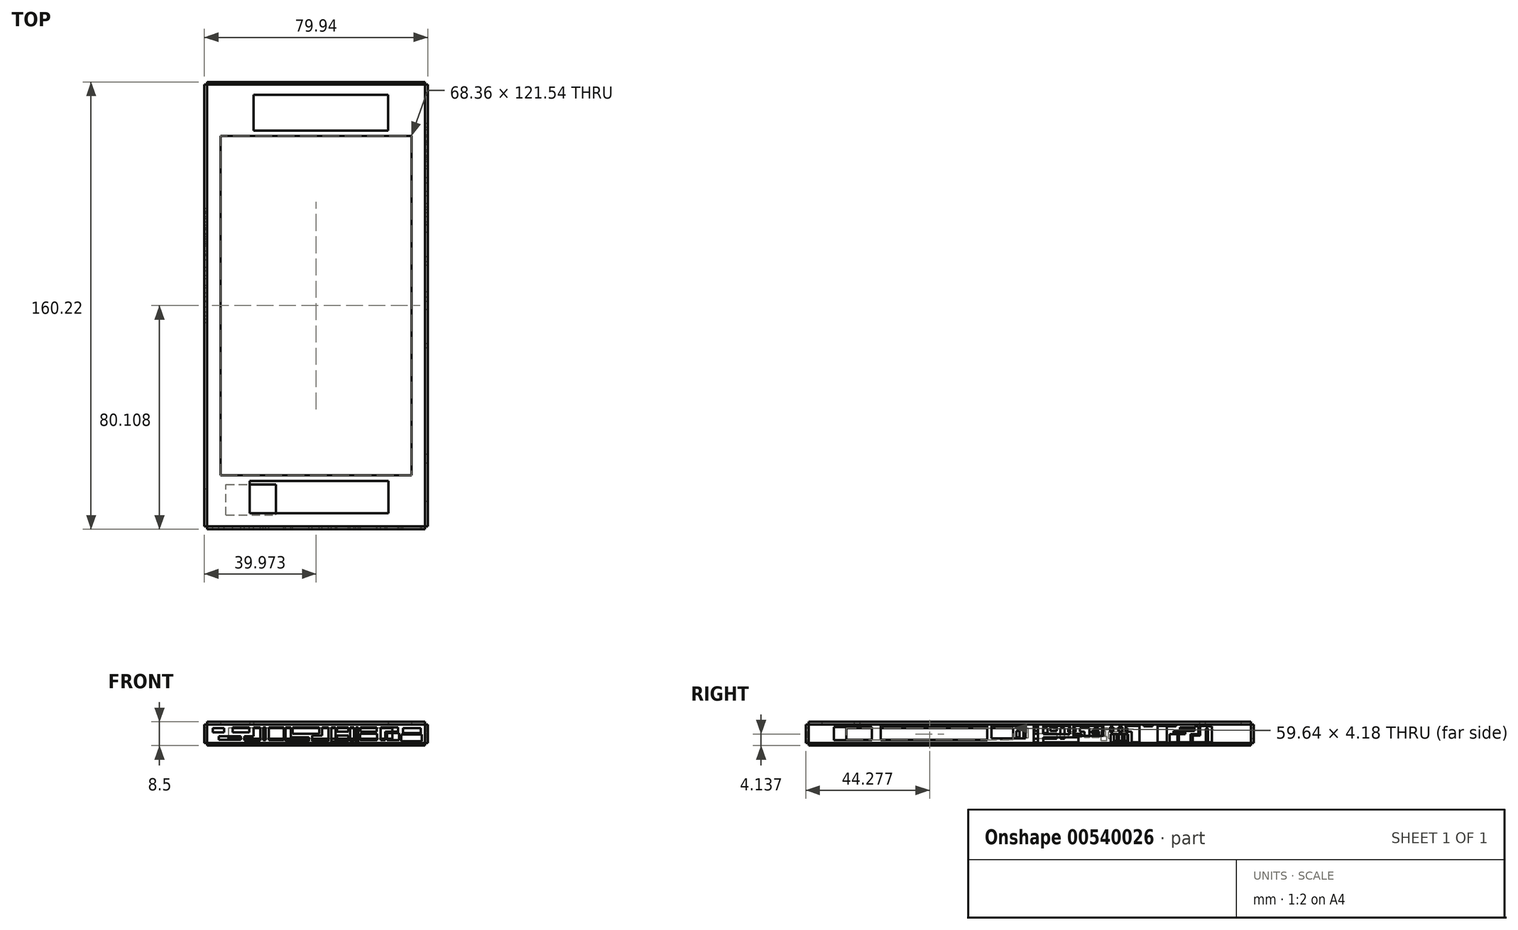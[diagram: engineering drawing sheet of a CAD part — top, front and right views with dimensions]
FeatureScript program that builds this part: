
annotation { "Feature Type Name" : "Feature", "Feature Type Description" : "" }
export const myFeature = defineFeature(function(context is Context, id is Id, definition is map)
    precondition{}
    {
        {
            var Q0;
            Q0=qCreatedBy(makeId("Top.planeOp"),FACE);
            var sketch = newSketch(context, id + "F0", { "sketchPlane" : qUnion([Q0])});
            skLineSegment(sketch, "E0.bottom", {"start": v(115.76, -47.1) * mm, "end": v(47.4, -47.1) * mm});
            skLineSegment(sketch, "E0.top", {"start": v(115.76, 74.45) * mm, "end": v(47.4, 74.45) * mm});
            skLineSegment(sketch, "E0.left", {"start": v(115.76, -47.1) * mm, "end": v(115.76, 74.45) * mm});
            skLineSegment(sketch, "E0.right", {"start": v(47.4, -47.1) * mm, "end": v(47.4, 74.45) * mm});
            skLineSegment(sketch, "E1.bottom", {"start": v(120.55, -65.43) * mm, "end": v(42.61, -65.43) * mm});
            skLineSegment(sketch, "E1.top", {"start": v(120.55, 92.79) * mm, "end": v(42.61, 92.79) * mm});
            skLineSegment(sketch, "E1.left", {"start": v(120.55, -65.43) * mm, "end": v(120.55, 92.79) * mm});
            skLineSegment(sketch, "E1.right", {"start": v(42.61, -65.43) * mm, "end": v(42.61, 92.79) * mm});
            skPoint(sketch, "E2", {"position": v(81.58, 13.68) * mm});
            skPoint(sketch, "E3", {"position": v(81.58, 74.45) * mm});
            skPoint(sketch, "E4", {"position": v(47.4, 13.68) * mm});
            skPoint(sketch, "E5", {"position": v(81.58, -65.43) * mm});
            skPoint(sketch, "E6", {"position": v(42.61, 13.68) * mm});
            skLineSegment(sketch, "E7.bottom", {"start": v(44.35, 91.05) * mm, "end": v(118.82, 91.05) * mm});
            skLineSegment(sketch, "E7.top", {"start": v(44.35, -63.7) * mm, "end": v(118.82, -63.7) * mm});
            skLineSegment(sketch, "E7.left", {"start": v(44.35, 91.05) * mm, "end": v(44.35, -63.7) * mm});
            skLineSegment(sketch, "E7.right", {"start": v(118.82, 91.05) * mm, "end": v(118.82, -63.7) * mm});
            skPoint(sketch, "E8", {"position": v(81.58, -63.7) * mm});
            skPoint(sketch, "E9", {"position": v(118.82, 13.68) * mm});
            skLineSegment(sketch, "E10.bottom", {"start": v(59.18, 89.21) * mm, "end": v(107.32, 89.21) * mm});
            skLineSegment(sketch, "E10.top", {"start": v(59.18, 76.37) * mm, "end": v(107.32, 76.37) * mm});
            skLineSegment(sketch, "E10.left", {"start": v(59.18, 89.21) * mm, "end": v(59.18, 76.37) * mm});
            skLineSegment(sketch, "E10.right", {"start": v(107.32, 89.21) * mm, "end": v(107.32, 76.37) * mm});
            skLineSegment(sketch, "E11.bottom", {"start": v(57.84, -49.13) * mm, "end": v(107.53, -49.13) * mm});
            skLineSegment(sketch, "E11.top", {"start": v(57.84, -60.7) * mm, "end": v(107.53, -60.7) * mm});
            skLineSegment(sketch, "E11.left", {"start": v(57.84, -49.13) * mm, "end": v(57.84, -60.7) * mm});
            skLineSegment(sketch, "E11.right", {"start": v(107.53, -49.13) * mm, "end": v(107.53, -60.7) * mm});
            skSolve(sketch);
        }
        {
            var Q0;
            Q0=makeQuery(id+"F0.imprint","IMPRINT",FACE,{"disambiguationData":[TD([[makeQuery(id+"F0.imprint","IMPRINT",EDGE,{"derivedFrom":sQuery(id+"F0.wireOp",EDGE,"E0.bottom")}),1.0]])]});
            var Q1;
            Q1=makeQuery(id+"F0.imprint","IMPRINT",FACE,{"disambiguationData":[TD([[makeQuery(id+"F0.imprint","IMPRINT",EDGE,{"derivedFrom":sQuery(id+"F0.wireOp",EDGE,"E1.bottom")}),-1.0]])]});
            extrude(context, id + "F1", {"entities" : qUnion([Q0, Q1]), "depth" : 1 * mm, "offsetDistance" : 25 * mm});
        }
        {
            var Q0;
            Q0=makeQuery(id+"F1.opExtrude","SWEPT_FACE",FACE,{"disambiguationData":[OSD([sQuery(id+"F0.wireOp",EDGE,"E1.left")])]});
            var sketch = newSketch(context, id + "F2", { "sketchPlane" : qUnion([Q0])});
            skLineSegment(sketch, "E12.bottom", {"start": v(-65.43, 1) * mm, "end": v(92.79, 1) * mm});
            skLineSegment(sketch, "E12.top", {"start": v(-65.43, -6.5) * mm, "end": v(92.79, -6.5) * mm});
            skLineSegment(sketch, "E12.left", {"start": v(-65.43, 1) * mm, "end": v(-65.43, -6.5) * mm});
            skLineSegment(sketch, "E12.right", {"start": v(92.79, 1) * mm, "end": v(92.79, -6.5) * mm});
            skLineSegment(sketch, "E13.bottom", {"start": v(-56.46, -0.8) * mm, "end": v(-42.84, -0.8) * mm});
            skLineSegment(sketch, "E13.top", {"start": v(-56.46, -5.5) * mm, "end": v(-42.84, -5.5) * mm});
            skLineSegment(sketch, "E13.left", {"start": v(-56.46, -0.8) * mm, "end": v(-56.46, -5.5) * mm});
            skLineSegment(sketch, "E13.right", {"start": v(-42.84, -0.8) * mm, "end": v(-42.84, -5.5) * mm});
            skLineSegment(sketch, "E14.bottom", {"start": v(-39.62, -0.51) * mm, "end": v(-1.52, -0.51) * mm});
            skLineSegment(sketch, "E14.top", {"start": v(-39.62, -5.6) * mm, "end": v(-1.52, -5.6) * mm});
            skLineSegment(sketch, "E14.left", {"start": v(-39.62, -0.51) * mm, "end": v(-39.62, -5.6) * mm});
            skLineSegment(sketch, "E14.right", {"start": v(-1.52, -0.51) * mm, "end": v(-1.52, -5.6) * mm});
            skLineSegment(sketch, "E15.bottom", {"start": v(0, -0.51) * mm, "end": v(12.2, -0.51) * mm});
            skLineSegment(sketch, "E15.top", {"start": v(0, -4.86) * mm, "end": v(12.2, -4.86) * mm});
            skLineSegment(sketch, "E15.left", {"start": v(0, -0.51) * mm, "end": v(0, -4.86) * mm});
            skLineSegment(sketch, "E15.right", {"start": v(12.2, -0.51) * mm, "end": v(12.2, -4.86) * mm});
            skLineSegment(sketch, "E16.bottom", {"start": v(15.07, -0.51) * mm, "end": v(16.6, -0.51) * mm});
            skLineSegment(sketch, "E16.top", {"start": v(15.07, -6.36) * mm, "end": v(16.6, -6.36) * mm});
            skLineSegment(sketch, "E16.left", {"start": v(15.07, -0.51) * mm, "end": v(15.07, -6.36) * mm});
            skLineSegment(sketch, "E16.right", {"start": v(16.6, -0.51) * mm, "end": v(16.6, -6.36) * mm});
            skLineSegment(sketch, "E17.bottom", {"start": v(18.51, -0.51) * mm, "end": v(28.08, -0.51) * mm});
            skLineSegment(sketch, "E17.top", {"start": v(18.51, -3.32) * mm, "end": v(28.08, -3.32) * mm});
            skLineSegment(sketch, "E17.left", {"start": v(18.51, -0.51) * mm, "end": v(18.51, -3.32) * mm});
            skLineSegment(sketch, "E17.right", {"start": v(28.08, -0.51) * mm, "end": v(28.08, -3.32) * mm});
            skLineSegment(sketch, "E18.bottom", {"start": v(18.51, -6.36) * mm, "end": v(31.14, -6.36) * mm});
            skLineSegment(sketch, "E18.top", {"start": v(18.51, -4.47) * mm, "end": v(31.14, -4.47) * mm});
            skLineSegment(sketch, "E18.left", {"start": v(18.51, -6.36) * mm, "end": v(18.51, -4.47) * mm});
            skLineSegment(sketch, "E18.right", {"start": v(31.14, -6.36) * mm, "end": v(31.14, -4.47) * mm});
            skLineSegment(sketch, "E19.bottom", {"start": v(29.37, -3.96) * mm, "end": v(39.95, -3.96) * mm});
            skLineSegment(sketch, "E19.top", {"start": v(29.37, -0.51) * mm, "end": v(39.95, -0.51) * mm});
            skLineSegment(sketch, "E19.left", {"start": v(29.37, -3.96) * mm, "end": v(29.37, -0.51) * mm});
            skLineSegment(sketch, "E19.right", {"start": v(39.95, -3.96) * mm, "end": v(39.95, -0.51) * mm});
            skLineSegment(sketch, "E20.bottom", {"start": v(42.63, -3.32) * mm, "end": v(48.85, -3.32) * mm});
            skLineSegment(sketch, "E20.top", {"start": v(42.63, -6.36) * mm, "end": v(48.85, -6.36) * mm});
            skLineSegment(sketch, "E20.left", {"start": v(42.63, -3.32) * mm, "end": v(42.63, -6.36) * mm});
            skLineSegment(sketch, "E20.right", {"start": v(48.85, -3.32) * mm, "end": v(48.85, -6.36) * mm});
            skLineSegment(sketch, "E21.bottom", {"start": v(42.43, -0.84) * mm, "end": v(43.58, -0.84) * mm});
            skLineSegment(sketch, "E21.top", {"start": v(42.43, -2.56) * mm, "end": v(43.58, -2.56) * mm});
            skLineSegment(sketch, "E21.left", {"start": v(42.43, -0.84) * mm, "end": v(42.43, -2.56) * mm});
            skLineSegment(sketch, "E21.right", {"start": v(43.58, -0.84) * mm, "end": v(43.58, -2.56) * mm});
            skLineSegment(sketch, "E22.bottom", {"start": v(45.5, -0.84) * mm, "end": v(46.84, -0.84) * mm});
            skLineSegment(sketch, "E22.top", {"start": v(45.5, -2.46) * mm, "end": v(46.84, -2.46) * mm});
            skLineSegment(sketch, "E22.left", {"start": v(45.5, -0.84) * mm, "end": v(45.5, -2.46) * mm});
            skLineSegment(sketch, "E22.right", {"start": v(46.84, -0.84) * mm, "end": v(46.84, -2.46) * mm});
            skLineSegment(sketch, "E23.bottom", {"start": v(47.98, -0.51) * mm, "end": v(52.96, -0.51) * mm});
            skLineSegment(sketch, "E23.top", {"start": v(47.98, -2.56) * mm, "end": v(52.96, -2.56) * mm});
            skLineSegment(sketch, "E23.left", {"start": v(47.98, -0.51) * mm, "end": v(47.98, -2.56) * mm});
            skLineSegment(sketch, "E23.right", {"start": v(52.96, -0.51) * mm, "end": v(52.96, -2.56) * mm});
            skLineSegment(sketch, "E24.top", {"start": v(52.96, -6.36) * mm, "end": v(50.18, -6.36) * mm});
            skLineSegment(sketch, "E24.left", {"start": v(52.96, -2.56) * mm, "end": v(52.96, -6.36) * mm});
            skLineSegment(sketch, "E24.right", {"start": v(50.18, -2.56) * mm, "end": v(50.18, -6.36) * mm});
            skLineSegment(sketch, "E25.bottom", {"start": v(54.46, -0.51) * mm, "end": v(57.6, -0.51) * mm});
            skLineSegment(sketch, "E25.top", {"start": v(54.46, -0.65) * mm, "end": v(57.6, -0.65) * mm});
            skLineSegment(sketch, "E25.left", {"start": v(54.46, -0.65) * mm, "end": v(54.46, -0.51) * mm});
            skLineSegment(sketch, "E25.right", {"start": v(57.6, -0.65) * mm, "end": v(57.6, -0.51) * mm});
            skLineSegment(sketch, "E26.top", {"start": v(54.46, -6.36) * mm, "end": v(57.6, -6.36) * mm});
            skLineSegment(sketch, "E26.left", {"start": v(54.46, -0.51) * mm, "end": v(54.46, -6.36) * mm});
            skLineSegment(sketch, "E26.right", {"start": v(57.6, -1.64) * mm, "end": v(57.6, -6.36) * mm});
            skLineSegment(sketch, "E27.bottom", {"start": v(59.39, -0.65) * mm, "end": v(65.96, -0.65) * mm});
            skLineSegment(sketch, "E27.top", {"start": v(59.39, -0.51) * mm, "end": v(65.96, -0.51) * mm});
            skLineSegment(sketch, "E27.left", {"start": v(59.39, -0.51) * mm, "end": v(59.39, -0.65) * mm});
            skLineSegment(sketch, "E27.right", {"start": v(65.96, -0.51) * mm, "end": v(65.96, -0.65) * mm});
            skPoint(sketch, "E28.oppositeSnap0", {"position": v(62.67, -0.51) * mm});
            skLineSegment(sketch, "E28.bottom", {"start": v(59.39, -0.51) * mm, "end": v(62.67, -0.51) * mm});
            skLineSegment(sketch, "E28.top", {"start": v(59.39, -6.36) * mm, "end": v(62.67, -6.36) * mm});
            skLineSegment(sketch, "E28.left", {"start": v(59.39, -0.51) * mm, "end": v(59.39, -6.36) * mm});
            skLineSegment(sketch, "E28.right", {"start": v(62.67, -0.51) * mm, "end": v(62.67, -6.36) * mm});
            skPoint(sketch, "E29.firstSnap0", {"position": v(62.67, -3.44) * mm});
            skLineSegment(sketch, "E29.bottom", {"start": v(63.68, -3.44) * mm, "end": v(66.53, -3.44) * mm});
            skLineSegment(sketch, "E29.top", {"start": v(63.68, -6.36) * mm, "end": v(66.53, -6.36) * mm});
            skLineSegment(sketch, "E29.left", {"start": v(63.68, -3.44) * mm, "end": v(63.68, -6.36) * mm});
            skLineSegment(sketch, "E29.right", {"start": v(66.53, -3.44) * mm, "end": v(66.53, -6.36) * mm});
            skPoint(sketch, "E30.firstSnap0", {"position": v(65.1, -3.44) * mm});
            skLineSegment(sketch, "E30.bottom", {"start": v(65.1, -2.3) * mm, "end": v(68.7, -2.3) * mm});
            skLineSegment(sketch, "E30.top", {"start": v(65.1, -3.15) * mm, "end": v(68.7, -3.15) * mm});
            skLineSegment(sketch, "E30.left", {"start": v(65.1, -2.3) * mm, "end": v(65.1, -3.15) * mm});
            skLineSegment(sketch, "E30.right", {"start": v(68.7, -2.3) * mm, "end": v(68.7, -3.15) * mm});
            skLineSegment(sketch, "E31.bottom", {"start": v(67.44, -0.96) * mm, "end": v(72.16, -0.96) * mm});
            skLineSegment(sketch, "E31.top", {"start": v(67.44, -1.88) * mm, "end": v(72.16, -1.88) * mm});
            skLineSegment(sketch, "E31.left", {"start": v(67.44, -0.96) * mm, "end": v(67.44, -1.88) * mm});
            skLineSegment(sketch, "E31.right", {"start": v(72.16, -0.96) * mm, "end": v(72.16, -1.88) * mm});
            skLineSegment(sketch, "E32.bottom", {"start": v(67, -3.44) * mm, "end": v(71.26, -3.44) * mm});
            skLineSegment(sketch, "E32.top", {"start": v(67, -6.36) * mm, "end": v(71.26, -6.36) * mm});
            skLineSegment(sketch, "E32.left", {"start": v(67, -3.44) * mm, "end": v(67, -6.36) * mm});
            skLineSegment(sketch, "E32.right", {"start": v(71.26, -3.44) * mm, "end": v(71.26, -6.36) * mm});
            skLineSegment(sketch, "E33.bottom", {"start": v(71.26, -3.44) * mm, "end": v(69.33, -3.44) * mm});
            skLineSegment(sketch, "E33.top", {"start": v(71.26, -2.22) * mm, "end": v(69.33, -2.22) * mm});
            skLineSegment(sketch, "E33.left", {"start": v(71.26, -3.44) * mm, "end": v(71.26, -2.22) * mm});
            skLineSegment(sketch, "E33.right", {"start": v(69.33, -3.44) * mm, "end": v(69.33, -2.22) * mm});
            skLineSegment(sketch, "E34.bottom", {"start": v(71.26, -2.22) * mm, "end": v(74.03, -2.22) * mm});
            skLineSegment(sketch, "E34.top", {"start": v(71.26, -3.44) * mm, "end": v(74.03, -3.44) * mm});
            skLineSegment(sketch, "E34.left", {"start": v(71.26, -2.22) * mm, "end": v(71.26, -3.44) * mm});
            skLineSegment(sketch, "E34.right", {"start": v(74.03, -2.22) * mm, "end": v(74.03, -3.44) * mm});
            skLineSegment(sketch, "E35.bottom", {"start": v(74.03, -2.22) * mm, "end": v(72.68, -2.22) * mm});
            skLineSegment(sketch, "E35.top", {"start": v(74.03, -0.65) * mm, "end": v(72.68, -0.65) * mm});
            skLineSegment(sketch, "E35.left", {"start": v(74.03, -2.22) * mm, "end": v(74.03, -0.65) * mm});
            skLineSegment(sketch, "E35.right", {"start": v(72.68, -2.22) * mm, "end": v(72.68, -0.65) * mm});
            skLineSegment(sketch, "E36.bottom", {"start": v(71.94, -3.84) * mm, "end": v(76.64, -3.84) * mm});
            skLineSegment(sketch, "E36.top", {"start": v(71.94, -6.36) * mm, "end": v(76.64, -6.36) * mm});
            skLineSegment(sketch, "E36.left", {"start": v(71.94, -3.84) * mm, "end": v(71.94, -6.36) * mm});
            skLineSegment(sketch, "E36.right", {"start": v(76.64, -3.84) * mm, "end": v(76.64, -6.36) * mm});
            skLineSegment(sketch, "E37.bottom", {"start": v(76.64, -3.84) * mm, "end": v(74.68, -3.84) * mm});
            skLineSegment(sketch, "E37.top", {"start": v(76.64, -0.51) * mm, "end": v(74.68, -0.51) * mm});
            skLineSegment(sketch, "E37.left", {"start": v(76.64, -3.84) * mm, "end": v(76.64, -0.51) * mm});
            skLineSegment(sketch, "E37.right", {"start": v(74.68, -3.84) * mm, "end": v(74.68, -0.51) * mm});
            skLineSegment(sketch, "E38.bottom", {"start": v(74.78, -0.65) * mm, "end": v(78.86, -0.65) * mm});
            skLineSegment(sketch, "E38.top", {"start": v(74.78, -1.36) * mm, "end": v(78.86, -1.36) * mm});
            skLineSegment(sketch, "E38.left", {"start": v(74.78, -0.65) * mm, "end": v(74.78, -1.36) * mm});
            skLineSegment(sketch, "E38.right", {"start": v(78.86, -0.65) * mm, "end": v(78.86, -1.36) * mm});
            skLineSegment(sketch, "E39.bottom", {"start": v(78.86, -1.36) * mm, "end": v(77.43, -1.36) * mm});
            skLineSegment(sketch, "E39.top", {"start": v(78.86, -6.36) * mm, "end": v(77.43, -6.36) * mm});
            skLineSegment(sketch, "E39.left", {"start": v(78.86, -1.36) * mm, "end": v(78.86, -6.36) * mm});
            skLineSegment(sketch, "E39.right", {"start": v(77.43, -1.36) * mm, "end": v(77.43, -6.36) * mm});
            skLineSegment(sketch, "E40.left", {"start": v(57.6, -2.82) * mm, "end": v(57.6, -3.84) * mm});
            skLineSegment(sketch, "E40.right", {"start": v(54.46, -2.82) * mm, "end": v(54.46, -3.84) * mm});
            skLineSegment(sketch, "E41.left", {"start": v(59.39, -2.82) * mm, "end": v(59.39, -4.47) * mm});
            skLineSegment(sketch, "E41.right", {"start": v(62.67, -2.82) * mm, "end": v(62.67, -4.47) * mm});
            skLineSegment(sketch, "E42.left", {"start": v(50.18, -3.44) * mm, "end": v(50.18, -4.47) * mm});
            skLineSegment(sketch, "E42.right", {"start": v(52.96, -3.44) * mm, "end": v(52.96, -4.47) * mm});
            skLineSegment(sketch, "E43.top", {"start": v(44.76, -6.36) * mm, "end": v(46.48, -6.36) * mm});
            skSolve(sketch);
        }
        {
            var Q0;
            Q0=makeQuery(id+"F1.opExtrude","SWEPT_FACE",FACE,{"disambiguationData":[OSD([sQuery(id+"F0.wireOp",EDGE,"E1.bottom")])]});
            var sketch = newSketch(context, id + "F3", { "sketchPlane" : qUnion([Q0])});
            skLineSegment(sketch, "E44.bottom", {"start": v(42.61, 1) * mm, "end": v(120.55, 1) * mm});
            skLineSegment(sketch, "E44.top", {"start": v(42.61, -6.5) * mm, "end": v(120.55, -6.5) * mm});
            skLineSegment(sketch, "E44.left", {"start": v(42.61, 1) * mm, "end": v(42.61, -6.5) * mm});
            skLineSegment(sketch, "E44.right", {"start": v(120.55, 1) * mm, "end": v(120.55, -6.5) * mm});
            skPoint(sketch, "E45.oppositeSnap0", {"position": v(42.61, -2.75) * mm});
            skLineSegment(sketch, "E45.bottom", {"start": v(44.66, -1.22) * mm, "end": v(48.72, -1.22) * mm});
            skLineSegment(sketch, "E45.top", {"start": v(44.66, -2.75) * mm, "end": v(48.72, -2.75) * mm});
            skLineSegment(sketch, "E45.left", {"start": v(44.66, -1.22) * mm, "end": v(44.66, -2.75) * mm});
            skLineSegment(sketch, "E45.right", {"start": v(48.72, -1.22) * mm, "end": v(48.72, -2.75) * mm});
            skLineSegment(sketch, "E46.bottom", {"start": v(46.74, -4.18) * mm, "end": v(54.64, -4.18) * mm});
            skLineSegment(sketch, "E46.top", {"start": v(46.74, -5.4) * mm, "end": v(54.64, -5.4) * mm});
            skLineSegment(sketch, "E46.left", {"start": v(46.74, -4.18) * mm, "end": v(46.74, -5.4) * mm});
            skLineSegment(sketch, "E46.right", {"start": v(54.64, -4.18) * mm, "end": v(54.64, -5.4) * mm});
            skLineSegment(sketch, "E47.bottom", {"start": v(51.79, -1) * mm, "end": v(57.7, -1) * mm});
            skLineSegment(sketch, "E47.top", {"start": v(51.79, -2.76) * mm, "end": v(57.7, -2.76) * mm});
            skLineSegment(sketch, "E47.left", {"start": v(51.79, -1) * mm, "end": v(51.79, -2.76) * mm});
            skLineSegment(sketch, "E47.right", {"start": v(57.7, -1) * mm, "end": v(57.7, -2.76) * mm});
            skLineSegment(sketch, "E48.bottom", {"start": v(55.95, -4.18) * mm, "end": v(61.65, -4.18) * mm});
            skLineSegment(sketch, "E48.top", {"start": v(55.95, -5.6) * mm, "end": v(61.65, -5.6) * mm});
            skLineSegment(sketch, "E48.left", {"start": v(55.95, -4.18) * mm, "end": v(55.95, -5.6) * mm});
            skLineSegment(sketch, "E48.right", {"start": v(61.65, -4.18) * mm, "end": v(61.65, -5.6) * mm});
            skLineSegment(sketch, "E49.bottom", {"start": v(61.65, -4.18) * mm, "end": v(59.24, -4.18) * mm});
            skLineSegment(sketch, "E49.top", {"start": v(61.65, -1) * mm, "end": v(59.24, -1) * mm});
            skLineSegment(sketch, "E49.left", {"start": v(61.65, -4.18) * mm, "end": v(61.65, -1) * mm});
            skLineSegment(sketch, "E49.right", {"start": v(59.24, -4.18) * mm, "end": v(59.24, -1) * mm});
            skLineSegment(sketch, "E50.bottom", {"start": v(64.72, -1) * mm, "end": v(69.99, -1) * mm});
            skLineSegment(sketch, "E50.top", {"start": v(64.72, -5.6) * mm, "end": v(69.99, -5.6) * mm});
            skLineSegment(sketch, "E50.left", {"start": v(64.72, -1) * mm, "end": v(64.72, -5.6) * mm});
            skLineSegment(sketch, "E50.right", {"start": v(69.99, -1) * mm, "end": v(69.99, -5.6) * mm});
            skLineSegment(sketch, "E51.bottom", {"start": v(62.64, -1) * mm, "end": v(63.52, -1) * mm});
            skLineSegment(sketch, "E51.top", {"start": v(62.64, -5.6) * mm, "end": v(63.52, -5.6) * mm});
            skLineSegment(sketch, "E51.left", {"start": v(62.64, -1) * mm, "end": v(62.64, -5.6) * mm});
            skLineSegment(sketch, "E51.right", {"start": v(63.52, -1) * mm, "end": v(63.52, -5.6) * mm});
            skPoint(sketch, "E52.oppositeSnap0", {"position": v(69.99, -3.3) * mm});
            skLineSegment(sketch, "E52.bottom", {"start": v(73.28, -1) * mm, "end": v(82.7, -1) * mm});
            skLineSegment(sketch, "E52.top", {"start": v(73.28, -3.3) * mm, "end": v(82.7, -3.3) * mm});
            skLineSegment(sketch, "E52.left", {"start": v(73.28, -1) * mm, "end": v(73.28, -3.3) * mm});
            skLineSegment(sketch, "E52.right", {"start": v(82.7, -1) * mm, "end": v(82.7, -3.3) * mm});
            skLineSegment(sketch, "E53.bottom", {"start": v(72.52, -1) * mm, "end": v(70.71, -1) * mm});
            skLineSegment(sketch, "E53.top", {"start": v(72.52, -3.3) * mm, "end": v(70.71, -3.3) * mm});
            skLineSegment(sketch, "E53.left", {"start": v(72.52, -1) * mm, "end": v(72.52, -3.3) * mm});
            skLineSegment(sketch, "E53.right", {"start": v(70.71, -1) * mm, "end": v(70.71, -3.3) * mm});
            skLineSegment(sketch, "E54.bottom", {"start": v(70.71, -3.3) * mm, "end": v(72.52, -3.3) * mm});
            skLineSegment(sketch, "E54.top", {"start": v(70.71, -4.53) * mm, "end": v(72.52, -4.53) * mm});
            skLineSegment(sketch, "E54.left", {"start": v(70.71, -3.3) * mm, "end": v(70.71, -4.53) * mm});
            skLineSegment(sketch, "E54.right", {"start": v(72.52, -3.3) * mm, "end": v(72.52, -4.53) * mm});
            skLineSegment(sketch, "E55.bottom", {"start": v(70.71, -4.53) * mm, "end": v(79.07, -4.53) * mm});
            skLineSegment(sketch, "E55.top", {"start": v(70.71, -5.9) * mm, "end": v(79.07, -5.9) * mm});
            skLineSegment(sketch, "E55.left", {"start": v(70.71, -4.53) * mm, "end": v(70.71, -5.9) * mm});
            skLineSegment(sketch, "E55.right", {"start": v(79.07, -4.53) * mm, "end": v(79.07, -5.9) * mm});
            skLineSegment(sketch, "E56.bottom", {"start": v(80.15, -3.84) * mm, "end": v(86.01, -3.84) * mm});
            skLineSegment(sketch, "E56.top", {"start": v(80.15, -5.99) * mm, "end": v(86.01, -5.99) * mm});
            skLineSegment(sketch, "E56.left", {"start": v(80.15, -3.84) * mm, "end": v(80.15, -5.99) * mm});
            skLineSegment(sketch, "E56.right", {"start": v(86.01, -3.84) * mm, "end": v(86.01, -5.99) * mm});
            skLineSegment(sketch, "E57.bottom", {"start": v(86.01, -3.84) * mm, "end": v(83.74, -3.84) * mm});
            skLineSegment(sketch, "E57.top", {"start": v(86.01, -1) * mm, "end": v(83.74, -1) * mm});
            skLineSegment(sketch, "E57.left", {"start": v(86.01, -3.84) * mm, "end": v(86.01, -1) * mm});
            skLineSegment(sketch, "E57.right", {"start": v(83.74, -3.84) * mm, "end": v(83.74, -1) * mm});
            skLineSegment(sketch, "E58.bottom", {"start": v(87.03, -1) * mm, "end": v(88.58, -1) * mm});
            skLineSegment(sketch, "E58.top", {"start": v(87.03, -6.05) * mm, "end": v(88.58, -6.05) * mm});
            skLineSegment(sketch, "E58.left", {"start": v(87.03, -1) * mm, "end": v(87.03, -6.05) * mm});
            skLineSegment(sketch, "E58.right", {"start": v(88.58, -1) * mm, "end": v(88.58, -6.05) * mm});
            skLineSegment(sketch, "E59.bottom", {"start": v(89.12, -1) * mm, "end": v(93.18, -1) * mm});
            skLineSegment(sketch, "E59.top", {"start": v(89.12, -2.52) * mm, "end": v(93.18, -2.52) * mm});
            skLineSegment(sketch, "E59.left", {"start": v(89.12, -1) * mm, "end": v(89.12, -2.52) * mm});
            skLineSegment(sketch, "E59.right", {"start": v(93.18, -1) * mm, "end": v(93.18, -2.52) * mm});
            skLineSegment(sketch, "E60.bottom", {"start": v(89.12, -3.84) * mm, "end": v(93.18, -3.84) * mm});
            skLineSegment(sketch, "E60.top", {"start": v(89.12, -5.93) * mm, "end": v(93.18, -5.93) * mm});
            skLineSegment(sketch, "E60.left", {"start": v(89.12, -3.84) * mm, "end": v(89.12, -5.93) * mm});
            skLineSegment(sketch, "E60.right", {"start": v(93.18, -3.84) * mm, "end": v(93.18, -5.93) * mm});
            skLineSegment(sketch, "E61.bottom", {"start": v(93.79, -1) * mm, "end": v(95.22, -1) * mm});
            skLineSegment(sketch, "E61.top", {"start": v(93.79, -5.97) * mm, "end": v(95.22, -5.97) * mm});
            skLineSegment(sketch, "E61.left", {"start": v(93.79, -1) * mm, "end": v(93.79, -5.97) * mm});
            skLineSegment(sketch, "E61.right", {"start": v(95.22, -1) * mm, "end": v(95.22, -5.97) * mm});
            skLineSegment(sketch, "E62.bottom", {"start": v(96.66, -1) * mm, "end": v(95.82, -1) * mm});
            skLineSegment(sketch, "E62.top", {"start": v(96.66, -6) * mm, "end": v(95.82, -6) * mm});
            skLineSegment(sketch, "E62.left", {"start": v(96.66, -1) * mm, "end": v(96.66, -6) * mm});
            skLineSegment(sketch, "E62.right", {"start": v(95.82, -1) * mm, "end": v(95.82, -6) * mm});
            skLineSegment(sketch, "E63.bottom", {"start": v(97.5, -1) * mm, "end": v(103.27, -1) * mm});
            skLineSegment(sketch, "E63.top", {"start": v(97.5, -2.52) * mm, "end": v(103.27, -2.52) * mm});
            skLineSegment(sketch, "E63.left", {"start": v(97.5, -1) * mm, "end": v(97.5, -2.52) * mm});
            skLineSegment(sketch, "E63.right", {"start": v(103.27, -1) * mm, "end": v(103.27, -2.52) * mm});
            skLineSegment(sketch, "E64.bottom", {"start": v(97.37, -3.3) * mm, "end": v(103.46, -3.3) * mm});
            skLineSegment(sketch, "E64.top", {"start": v(97.37, -5.51) * mm, "end": v(103.46, -5.51) * mm});
            skLineSegment(sketch, "E64.left", {"start": v(97.37, -3.3) * mm, "end": v(97.37, -5.51) * mm});
            skLineSegment(sketch, "E64.right", {"start": v(103.46, -3.3) * mm, "end": v(103.46, -5.51) * mm});
            skLineSegment(sketch, "E65.bottom", {"start": v(99.4, -3.3) * mm, "end": v(101.34, -3.3) * mm});
            skLineSegment(sketch, "E65.top", {"start": v(99.4, -5.51) * mm, "end": v(101.34, -5.51) * mm});
            skLineSegment(sketch, "E65.left", {"start": v(99.4, -3.3) * mm, "end": v(99.4, -5.51) * mm});
            skLineSegment(sketch, "E65.right", {"start": v(101.34, -3.3) * mm, "end": v(101.34, -5.51) * mm});
            skLineSegment(sketch, "E66.bottom", {"start": v(104.76, -1) * mm, "end": v(106.42, -1) * mm});
            skLineSegment(sketch, "E66.top", {"start": v(104.76, -5.51) * mm, "end": v(106.42, -5.51) * mm});
            skLineSegment(sketch, "E66.left", {"start": v(104.76, -1) * mm, "end": v(104.76, -5.51) * mm});
            skLineSegment(sketch, "E66.right", {"start": v(106.42, -1) * mm, "end": v(106.42, -5.51) * mm});
            skLineSegment(sketch, "E67.bottom", {"start": v(106.42, -1) * mm, "end": v(110.87, -1) * mm});
            skLineSegment(sketch, "E67.top", {"start": v(106.42, -2.52) * mm, "end": v(110.87, -2.52) * mm});
            skLineSegment(sketch, "E67.left", {"start": v(106.42, -1) * mm, "end": v(106.42, -2.52) * mm});
            skLineSegment(sketch, "E67.right", {"start": v(110.87, -1) * mm, "end": v(110.87, -2.52) * mm});
            skLineSegment(sketch, "E68.bottom", {"start": v(106.97, -3.03) * mm, "end": v(111.35, -3.03) * mm});
            skLineSegment(sketch, "E68.top", {"start": v(106.97, -5.51) * mm, "end": v(111.35, -5.51) * mm});
            skLineSegment(sketch, "E68.left", {"start": v(106.97, -3.03) * mm, "end": v(106.97, -5.51) * mm});
            skLineSegment(sketch, "E68.right", {"start": v(111.35, -3.03) * mm, "end": v(111.35, -5.51) * mm});
            skLineSegment(sketch, "E69.bottom", {"start": v(112.74, -1.18) * mm, "end": v(119, -1.18) * mm});
            skLineSegment(sketch, "E69.top", {"start": v(112.74, -3.03) * mm, "end": v(119, -3.03) * mm});
            skLineSegment(sketch, "E69.left", {"start": v(112.74, -1.18) * mm, "end": v(112.74, -3.03) * mm});
            skLineSegment(sketch, "E69.right", {"start": v(119, -1.18) * mm, "end": v(119, -3.03) * mm});
            skLineSegment(sketch, "E70.bottom", {"start": v(112.07, -3.56) * mm, "end": v(119.38, -3.56) * mm});
            skLineSegment(sketch, "E70.top", {"start": v(112.07, -5.93) * mm, "end": v(119.38, -5.93) * mm});
            skLineSegment(sketch, "E70.left", {"start": v(112.07, -3.56) * mm, "end": v(112.07, -5.93) * mm});
            skLineSegment(sketch, "E70.right", {"start": v(119.38, -3.56) * mm, "end": v(119.38, -5.93) * mm});
            skSolve(sketch);
        }
        {
            var Q0;
            {var subQ4=sQuery(id+"F2.wireOp",EDGE,"E12.top");Q0=makeQuery(id+"F2.imprint","IMPRINT",FACE,{"disambiguationData":[TD([[makeQuery(id+"F2.imprint","IMPRINT",EDGE,{"derivedFrom":subQ4}),1.0]])]});}
            extrude(context, id + "F4", {"entities" : qUnion([Q0]), "depth" : 1 * mm, "offsetDistance" : 25 * mm});
        }
        {
            var Q0;
            Q0=makeQuery(id+"F1.opExtrude","SWEPT_FACE",FACE,{"disambiguationData":[OSD([sQuery(id+"F0.wireOp",EDGE,"E1.right")])]});
            var sketch = newSketch(context, id + "F5", { "sketchPlane" : qUnion([Q0])});
            skLineSegment(sketch, "E71.bottom", {"start": v(-92.79, 1) * mm, "end": v(65.43, 1) * mm});
            skLineSegment(sketch, "E71.top", {"start": v(-92.79, -6.5) * mm, "end": v(65.43, -6.5) * mm});
            skLineSegment(sketch, "E71.left", {"start": v(-92.79, 1) * mm, "end": v(-92.79, -6.5) * mm});
            skLineSegment(sketch, "E71.right", {"start": v(65.43, 1) * mm, "end": v(65.43, -6.5) * mm});
            skLineSegment(sketch, "E72.bottom", {"start": v(51.97, -5.45) * mm, "end": v(-7.67, -5.45) * mm});
            skLineSegment(sketch, "E72.top", {"start": v(51.97, -1.27) * mm, "end": v(-7.67, -1.27) * mm});
            skLineSegment(sketch, "E72.left", {"start": v(51.97, -5.45) * mm, "end": v(51.97, -1.27) * mm});
            skLineSegment(sketch, "E72.right", {"start": v(-7.67, -5.45) * mm, "end": v(-7.67, -1.27) * mm});
            skLineSegment(sketch, "E73.bottom", {"start": v(-23.32, -3.32) * mm, "end": v(-15.08, -3.32) * mm});
            skLineSegment(sketch, "E73.top", {"start": v(-23.32, -5.03) * mm, "end": v(-15.08, -5.03) * mm});
            skLineSegment(sketch, "E73.left", {"start": v(-23.32, -3.32) * mm, "end": v(-23.32, -5.03) * mm});
            skLineSegment(sketch, "E73.right", {"start": v(-15.08, -3.32) * mm, "end": v(-15.08, -5.03) * mm});
            skLineSegment(sketch, "E74.bottom", {"start": v(-11.45, -4.65) * mm, "end": v(-13.16, -4.65) * mm});
            skLineSegment(sketch, "E74.top", {"start": v(-11.45, -1.27) * mm, "end": v(-13.16, -1.27) * mm});
            skLineSegment(sketch, "E74.left", {"start": v(-11.45, -4.65) * mm, "end": v(-11.45, -1.27) * mm});
            skLineSegment(sketch, "E74.right", {"start": v(-13.16, -4.65) * mm, "end": v(-13.16, -1.27) * mm});
            skLineSegment(sketch, "E75.bottom", {"start": v(-9.98, -2.2) * mm, "end": v(-8.84, -2.2) * mm});
            skLineSegment(sketch, "E75.top", {"start": v(-9.98, -4.5) * mm, "end": v(-8.84, -4.5) * mm});
            skLineSegment(sketch, "E75.left", {"start": v(-9.98, -2.2) * mm, "end": v(-9.98, -4.5) * mm});
            skLineSegment(sketch, "E75.right", {"start": v(-8.84, -2.2) * mm, "end": v(-8.84, -4.5) * mm});
            skPoint(sketch, "E76.firstSnap0", {"position": v(-9.41, -2.2) * mm});
            skLineSegment(sketch, "E76.bottom", {"start": v(-15.39, -2.2) * mm, "end": v(-16.9, -2.2) * mm});
            skLineSegment(sketch, "E76.top", {"start": v(-15.39, -0.87) * mm, "end": v(-16.9, -0.87) * mm});
            skLineSegment(sketch, "E76.left", {"start": v(-15.39, -2.2) * mm, "end": v(-15.39, -0.87) * mm});
            skLineSegment(sketch, "E76.right", {"start": v(-16.9, -2.2) * mm, "end": v(-16.9, -0.87) * mm});
            skLineSegment(sketch, "E77.bottom", {"start": v(-18.25, -2.96) * mm, "end": v(-20.06, -2.96) * mm});
            skLineSegment(sketch, "E77.top", {"start": v(-18.25, -1.27) * mm, "end": v(-20.06, -1.27) * mm});
            skLineSegment(sketch, "E77.left", {"start": v(-18.25, -2.96) * mm, "end": v(-18.25, -1.27) * mm});
            skLineSegment(sketch, "E77.right", {"start": v(-20.06, -2.96) * mm, "end": v(-20.06, -1.27) * mm});
            skLineSegment(sketch, "E78.bottom", {"start": v(-23.32, -2.3) * mm, "end": v(-21.01, -2.3) * mm});
            skLineSegment(sketch, "E78.top", {"start": v(-23.32, -0.92) * mm, "end": v(-21.01, -0.92) * mm});
            skLineSegment(sketch, "E78.left", {"start": v(-23.32, -2.3) * mm, "end": v(-23.32, -0.92) * mm});
            skLineSegment(sketch, "E78.right", {"start": v(-21.01, -2.3) * mm, "end": v(-21.01, -0.92) * mm});
            skLineSegment(sketch, "E79.bottom", {"start": v(-24.58, -5.08) * mm, "end": v(-26.14, -5.08) * mm});
            skLineSegment(sketch, "E79.top", {"start": v(-24.58, -1.27) * mm, "end": v(-26.14, -1.27) * mm});
            skLineSegment(sketch, "E79.left", {"start": v(-24.58, -5.08) * mm, "end": v(-24.58, -1.27) * mm});
            skLineSegment(sketch, "E79.right", {"start": v(-26.14, -5.08) * mm, "end": v(-26.14, -1.27) * mm});
            skLineSegment(sketch, "E80.bottom", {"start": v(-32.2, -4.58) * mm, "end": v(-27.5, -4.58) * mm});
            skLineSegment(sketch, "E80.top", {"start": v(-32.2, -3.32) * mm, "end": v(-27.5, -3.32) * mm});
            skLineSegment(sketch, "E80.left", {"start": v(-32.2, -4.58) * mm, "end": v(-32.2, -3.32) * mm});
            skLineSegment(sketch, "E80.right", {"start": v(-27.5, -4.58) * mm, "end": v(-27.5, -3.32) * mm});
            skLineSegment(sketch, "E81.bottom", {"start": v(-30.12, -1.27) * mm, "end": v(-27.44, -1.27) * mm});
            skLineSegment(sketch, "E81.top", {"start": v(-30.12, -2.66) * mm, "end": v(-27.44, -2.66) * mm});
            skLineSegment(sketch, "E81.left", {"start": v(-30.12, -1.27) * mm, "end": v(-30.12, -2.66) * mm});
            skLineSegment(sketch, "E81.right", {"start": v(-27.44, -1.27) * mm, "end": v(-27.44, -2.66) * mm});
            skLineSegment(sketch, "E82.bottom", {"start": v(-31.64, -1.27) * mm, "end": v(-35.02, -1.27) * mm});
            skLineSegment(sketch, "E82.top", {"start": v(-31.64, -2.5) * mm, "end": v(-35.02, -2.5) * mm});
            skLineSegment(sketch, "E82.left", {"start": v(-31.64, -1.27) * mm, "end": v(-31.64, -2.5) * mm});
            skLineSegment(sketch, "E82.right", {"start": v(-35.02, -1.27) * mm, "end": v(-35.02, -2.5) * mm});
            skLineSegment(sketch, "E83.bottom", {"start": v(-35.02, -2.5) * mm, "end": v(-33.26, -2.5) * mm});
            skLineSegment(sketch, "E83.top", {"start": v(-35.02, -4.66) * mm, "end": v(-33.26, -4.66) * mm});
            skLineSegment(sketch, "E83.left", {"start": v(-35.02, -2.5) * mm, "end": v(-35.02, -4.66) * mm});
            skLineSegment(sketch, "E83.right", {"start": v(-33.26, -2.5) * mm, "end": v(-33.26, -4.66) * mm});
            skPoint(sketch, "E84.firstSnap0", {"position": v(-31.64, -1.89) * mm});
            skLineSegment(sketch, "E84.bottom", {"start": v(-36.68, -1.89) * mm, "end": v(-38.4, -1.89) * mm});
            skLineSegment(sketch, "E84.top", {"start": v(-36.68, -1.27) * mm, "end": v(-38.4, -1.27) * mm});
            skLineSegment(sketch, "E84.left", {"start": v(-36.68, -1.89) * mm, "end": v(-36.68, -1.27) * mm});
            skLineSegment(sketch, "E84.right", {"start": v(-38.4, -1.89) * mm, "end": v(-38.4, -1.27) * mm});
            skLineSegment(sketch, "E85.bottom", {"start": v(-37.52, -3.06) * mm, "end": v(-35.74, -3.06) * mm});
            skLineSegment(sketch, "E85.top", {"start": v(-37.52, -2.2) * mm, "end": v(-35.74, -2.2) * mm});
            skLineSegment(sketch, "E85.left", {"start": v(-37.52, -3.06) * mm, "end": v(-37.52, -2.2) * mm});
            skLineSegment(sketch, "E85.right", {"start": v(-35.74, -3.06) * mm, "end": v(-35.74, -2.2) * mm});
            skLineSegment(sketch, "E86.bottom", {"start": v(-38.47, -2.32) * mm, "end": v(-37.77, -2.32) * mm});
            skLineSegment(sketch, "E86.top", {"start": v(-38.47, -4.65) * mm, "end": v(-37.77, -4.65) * mm});
            skLineSegment(sketch, "E86.left", {"start": v(-38.47, -2.32) * mm, "end": v(-38.47, -4.65) * mm});
            skLineSegment(sketch, "E86.right", {"start": v(-37.77, -2.32) * mm, "end": v(-37.77, -4.65) * mm});
            skLineSegment(sketch, "E87.bottom", {"start": v(-37.77, -4.65) * mm, "end": v(-36.05, -4.65) * mm});
            skLineSegment(sketch, "E87.top", {"start": v(-37.77, -3.64) * mm, "end": v(-36.05, -3.64) * mm});
            skLineSegment(sketch, "E87.left", {"start": v(-37.77, -4.65) * mm, "end": v(-37.77, -3.64) * mm});
            skLineSegment(sketch, "E87.right", {"start": v(-36.05, -4.65) * mm, "end": v(-36.05, -3.64) * mm});
            skLineSegment(sketch, "E88.bottom", {"start": v(-40.85, -3.9) * mm, "end": v(-39.54, -3.9) * mm});
            skLineSegment(sketch, "E88.top", {"start": v(-40.85, -2.32) * mm, "end": v(-39.54, -2.32) * mm});
            skLineSegment(sketch, "E88.left", {"start": v(-40.85, -3.9) * mm, "end": v(-40.85, -2.32) * mm});
            skLineSegment(sketch, "E88.right", {"start": v(-39.54, -3.9) * mm, "end": v(-39.54, -2.32) * mm});
            skLineSegment(sketch, "E89.bottom", {"start": v(-41.64, -1.27) * mm, "end": v(-39.24, -1.27) * mm});
            skLineSegment(sketch, "E89.top", {"start": v(-41.64, -1.89) * mm, "end": v(-39.24, -1.89) * mm});
            skLineSegment(sketch, "E89.left", {"start": v(-41.64, -1.27) * mm, "end": v(-41.64, -1.89) * mm});
            skLineSegment(sketch, "E89.right", {"start": v(-39.24, -1.27) * mm, "end": v(-39.24, -1.89) * mm});
            skLineSegment(sketch, "E90.bottom", {"start": v(-41.7, -2.66) * mm, "end": v(-42.59, -2.66) * mm});
            skLineSegment(sketch, "E90.top", {"start": v(-41.7, -4.92) * mm, "end": v(-42.59, -4.92) * mm});
            skLineSegment(sketch, "E90.left", {"start": v(-41.7, -2.66) * mm, "end": v(-41.7, -4.92) * mm});
            skLineSegment(sketch, "E90.right", {"start": v(-42.59, -2.66) * mm, "end": v(-42.59, -4.92) * mm});
            skLineSegment(sketch, "E91.bottom", {"start": v(-41.27, -5.83) * mm, "end": v(-39.24, -5.83) * mm});
            skLineSegment(sketch, "E91.top", {"start": v(-41.27, -4.33) * mm, "end": v(-39.24, -4.33) * mm});
            skLineSegment(sketch, "E91.left", {"start": v(-41.27, -5.83) * mm, "end": v(-41.27, -4.33) * mm});
            skLineSegment(sketch, "E91.right", {"start": v(-39.24, -5.83) * mm, "end": v(-39.24, -4.33) * mm});
            skLineSegment(sketch, "E92.bottom", {"start": v(-42.52, -1.27) * mm, "end": v(-45, -1.27) * mm});
            skLineSegment(sketch, "E92.top", {"start": v(-42.52, -2.32) * mm, "end": v(-45, -2.32) * mm});
            skLineSegment(sketch, "E92.left", {"start": v(-42.52, -1.27) * mm, "end": v(-42.52, -2.32) * mm});
            skLineSegment(sketch, "E92.right", {"start": v(-45, -1.27) * mm, "end": v(-45, -2.32) * mm});
            skLineSegment(sketch, "E93.bottom", {"start": v(-43.74, -3.06) * mm, "end": v(-44.81, -3.06) * mm});
            skLineSegment(sketch, "E93.top", {"start": v(-43.74, -5.76) * mm, "end": v(-44.81, -5.76) * mm});
            skLineSegment(sketch, "E93.left", {"start": v(-43.74, -3.06) * mm, "end": v(-43.74, -5.76) * mm});
            skLineSegment(sketch, "E93.right", {"start": v(-44.81, -3.06) * mm, "end": v(-44.81, -5.76) * mm});
            skPoint(sketch, "E94.firstSnap0", {"position": v(-43.76, -1.27) * mm});
            skLineSegment(sketch, "E94.bottom", {"start": v(-46.7, -1.27) * mm, "end": v(-45.62, -1.27) * mm});
            skLineSegment(sketch, "E94.top", {"start": v(-46.7, -5.86) * mm, "end": v(-45.62, -5.86) * mm});
            skLineSegment(sketch, "E94.left", {"start": v(-46.7, -1.27) * mm, "end": v(-46.7, -5.86) * mm});
            skLineSegment(sketch, "E94.right", {"start": v(-45.62, -1.27) * mm, "end": v(-45.62, -5.86) * mm});
            skLineSegment(sketch, "E95.bottom", {"start": v(-47.55, -1.27) * mm, "end": v(-48.58, -1.27) * mm});
            skLineSegment(sketch, "E95.top", {"start": v(-47.55, -5.86) * mm, "end": v(-48.58, -5.86) * mm});
            skLineSegment(sketch, "E95.left", {"start": v(-47.55, -1.27) * mm, "end": v(-47.55, -5.86) * mm});
            skLineSegment(sketch, "E95.right", {"start": v(-48.58, -1.27) * mm, "end": v(-48.58, -5.86) * mm});
            skLineSegment(sketch, "E96.bottom", {"start": v(-47.32, -4.3) * mm, "end": v(-47, -4.3) * mm});
            skLineSegment(sketch, "E96.top", {"start": v(-47.32, -2.5) * mm, "end": v(-47, -2.5) * mm});
            skLineSegment(sketch, "E96.left", {"start": v(-47.32, -4.3) * mm, "end": v(-47.32, -2.5) * mm});
            skLineSegment(sketch, "E96.right", {"start": v(-47, -4.3) * mm, "end": v(-47, -2.5) * mm});
            skSolve(sketch);
        }
        {
            var Q0;
            Q0=makeQuery(id+"F1.opExtrude","SWEPT_FACE",FACE,{"disambiguationData":[OSD([sQuery(id+"F0.wireOp",EDGE,"E1.top")])]});
            var sketch = newSketch(context, id + "F6", { "sketchPlane" : qUnion([Q0])});
            skLineSegment(sketch, "E97.bottom", {"start": v(-120.55, 1) * mm, "end": v(-42.61, 1) * mm});
            skLineSegment(sketch, "E97.top", {"start": v(-120.55, -6.5) * mm, "end": v(-42.61, -6.5) * mm});
            skLineSegment(sketch, "E97.left", {"start": v(-120.55, 1) * mm, "end": v(-120.55, -6.5) * mm});
            skLineSegment(sketch, "E97.right", {"start": v(-42.61, 1) * mm, "end": v(-42.61, -6.5) * mm});
            skLineSegment(sketch, "E98.bottom", {"start": v(-108.9, -1.22) * mm, "end": v(-50.29, -1.22) * mm});
            skLineSegment(sketch, "E98.top", {"start": v(-108.9, -5) * mm, "end": v(-50.29, -5) * mm});
            skLineSegment(sketch, "E98.left", {"start": v(-108.9, -1.22) * mm, "end": v(-108.9, -5) * mm});
            skLineSegment(sketch, "E98.right", {"start": v(-50.29, -1.22) * mm, "end": v(-50.29, -5) * mm});
            skSolve(sketch);
        }
        {
            var Q0;
            {var subQ0=sQuery(id+"F6.wireOp",EDGE,"E97.top");Q0=makeQuery(id+"F6.imprint","IMPRINT",FACE,{"disambiguationData":[TD([[makeQuery(id+"F6.imprint","IMPRINT",EDGE,{"derivedFrom":subQ0}),1.0]])]});}
            extrude(context, id + "F7", {"entities" : qUnion([Q0]), "depth" : 1 * mm, "offsetDistance" : 25 * mm});
        }
        {
            var Q0;
            {var subQ0=sQuery(id+"F5.wireOp",EDGE,"E71.top");Q0=makeQuery(id+"F5.imprint","IMPRINT",FACE,{"disambiguationData":[TD([[makeQuery(id+"F5.imprint","IMPRINT",EDGE,{"derivedFrom":subQ0}),1.0]])]});}
            extrude(context, id + "F8", {"entities" : qUnion([Q0]), "depth" : 1 * mm, "offsetDistance" : 25 * mm});
        }
        {
            var Q0;
            {var subQ0=sQuery(id+"F3.wireOp",EDGE,"E44.top");Q0=makeQuery(id+"F3.imprint","IMPRINT",FACE,{"disambiguationData":[TD([[makeQuery(id+"F3.imprint","IMPRINT",EDGE,{"derivedFrom":subQ0}),1.0]])]});}
            extrude(context, id + "F9", {"entities" : qUnion([Q0]), "depth" : 1 * mm, "offsetDistance" : 25 * mm});
        }
        {
            var Q0;
            Q0=makeQuery(id+"F8.opExtrude","SWEPT_FACE",FACE,{"disambiguationData":[OSD([sQuery(id+"F5.wireOp",EDGE,"E71.top")])]});
            var sketch = newSketch(context, id + "F10", { "sketchPlane" : qUnion([Q0])});
            skLineSegment(sketch, "E99.bottom", {"start": v(42.61, 65.43) * mm, "end": v(120.55, 65.43) * mm});
            skLineSegment(sketch, "E99.top", {"start": v(42.61, -92.79) * mm, "end": v(120.55, -92.79) * mm});
            skLineSegment(sketch, "E99.left", {"start": v(42.61, 65.43) * mm, "end": v(42.61, -92.79) * mm});
            skLineSegment(sketch, "E99.right", {"start": v(120.55, 65.43) * mm, "end": v(120.55, -92.79) * mm});
            skLineSegment(sketch, "E100.bottom", {"start": v(49.36, 61.4) * mm, "end": v(67.18, 61.4) * mm});
            skLineSegment(sketch, "E100.top", {"start": v(49.36, 50.4) * mm, "end": v(67.18, 50.4) * mm});
            skLineSegment(sketch, "E100.left", {"start": v(49.36, 61.4) * mm, "end": v(49.36, 50.4) * mm});
            skLineSegment(sketch, "E100.right", {"start": v(67.18, 61.4) * mm, "end": v(67.18, 50.4) * mm});
            skSolve(sketch);
        }
        {
            var Q0;
            Q0=makeQuery(id+"F10.imprint","IMPRINT",FACE,{"disambiguationData":[TD([[makeQuery(id+"F10.imprint","IMPRINT",EDGE,{"derivedFrom":sQuery(id+"F10.wireOp",EDGE,"E99.bottom")}),-1.0]])]});
            extrude(context, id + "F11", {"entities" : qUnion([Q0]), "operationType" : NewBodyOperationType.ADD, "depth" : 1 * mm, "offsetDistance" : 25 * mm});
        }
    });
